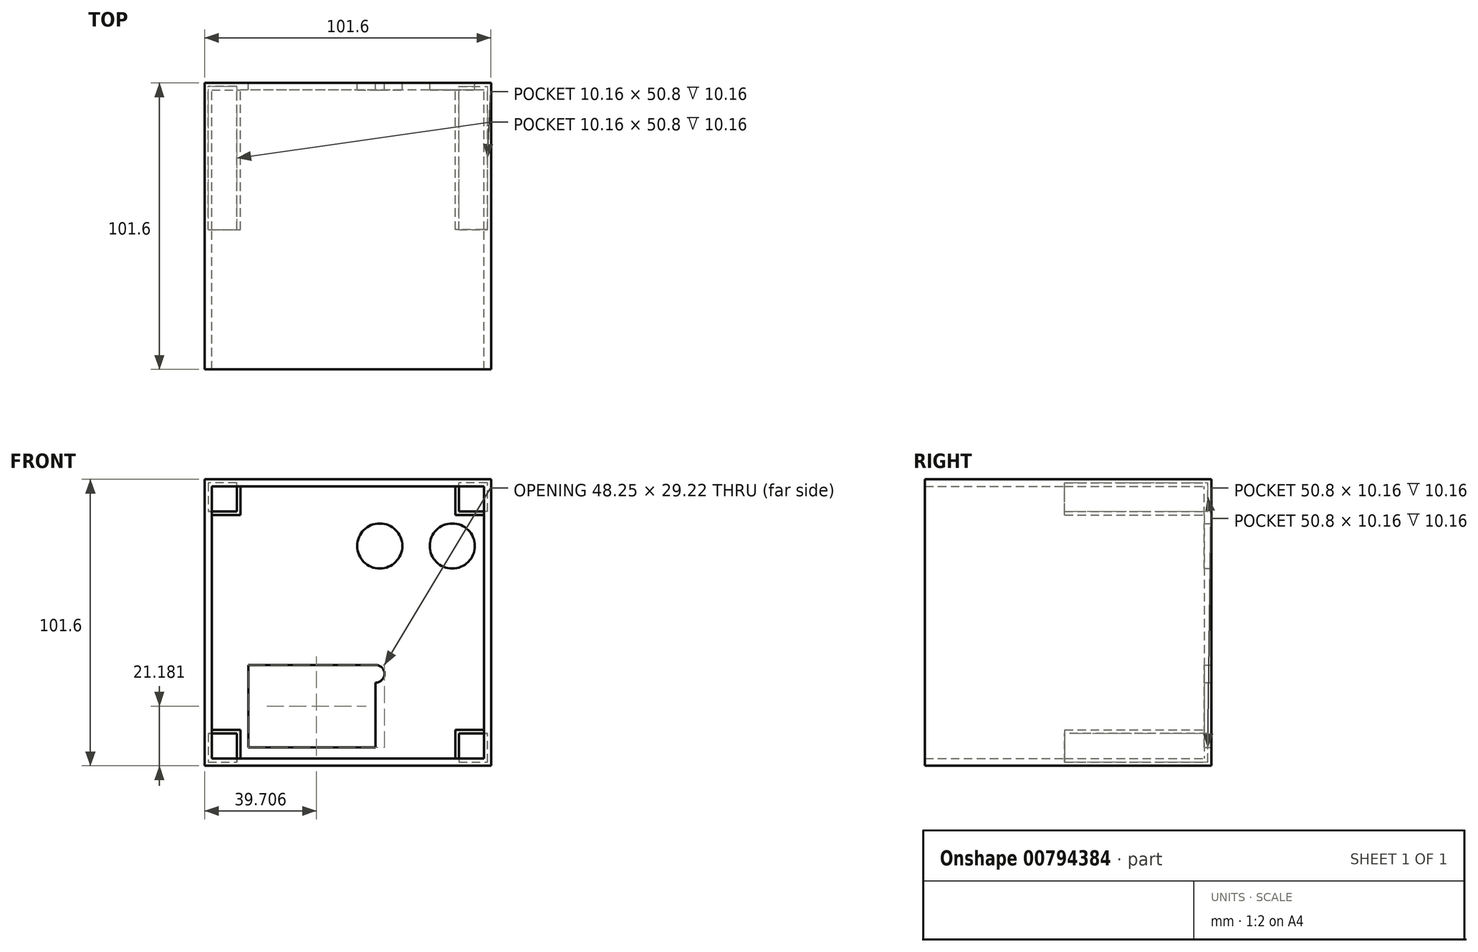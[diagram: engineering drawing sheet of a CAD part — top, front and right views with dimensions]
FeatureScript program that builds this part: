
annotation { "Feature Type Name" : "Feature", "Feature Type Description" : "" }
export const myFeature = defineFeature(function(context is Context, id is Id, definition is map)
    precondition{}
    {
        {
            var Q0;
            Q0=qCreatedBy(makeId("Front.planeOp"),FACE);
            var sketch = newSketch(context, id + "F0", { "sketchPlane" : qUnion([Q0])});
            skLineSegment(sketch, "E0", {"start": v(-90.78, 89.85) * mm, "end": v(-90.78, -11.75) * mm});
            skLineSegment(sketch, "E1", {"start": v(-90.78, -11.75) * mm, "end": v(10.82, -11.75) * mm});
            skLineSegment(sketch, "E2", {"start": v(10.82, -11.75) * mm, "end": v(10.82, 89.85) * mm});
            skLineSegment(sketch, "E3", {"start": v(10.82, 89.85) * mm, "end": v(-90.78, 89.85) * mm});
            skCircle(sketch, "E4", {"center": v(-28.63, 66.22) * mm, "radius": 8 * mm});
            skCircle(sketch, "E5", {"center": v(-2.9, 66.22) * mm, "radius": 8 * mm});
            skLineSegment(sketch, "E6", {"start": v(-75.2, 24.04) * mm, "end": v(-75.2, -5.18) * mm});
            skLineSegment(sketch, "E7", {"start": v(-75.2, -5.18) * mm, "end": v(-30.1, -5.18) * mm});
            skLineSegment(sketch, "E8", {"start": v(-30.1, -5.18) * mm, "end": v(-30.1, 24.04) * mm});
            skLineSegment(sketch, "E9", {"start": v(-30.1, 24.04) * mm, "end": v(-75.2, 24.04) * mm});
            skArc(sketch, "E10", {"start": v(-30.1, 17.74) * mm, "mid": v(-26.95, 20.9) * mm, "end": v(-30.1, 24.04) * mm});
            skLineSegment(sketch, "E11", {"start": v(-90.78, 77.15) * mm, "end": v(-78.08, 77.15) * mm});
            skLineSegment(sketch, "E12", {"start": v(-78.08, 77.15) * mm, "end": v(-78.08, 89.85) * mm});
            skLineSegment(sketch, "E13", {"start": v(-39.98, 89.85) * mm, "end": v(-39.98, -11.75) * mm, "construction": true});
            skLineSegment(sketch, "E14.MirrorCS", {"start": v(-1.88, 77.15) * mm, "end": v(-1.88, 89.85) * mm});
            skLineSegment(sketch, "E15.MirrorCS", {"start": v(10.82, 77.15) * mm, "end": v(-1.88, 77.15) * mm});
            skLineSegment(sketch, "E16", {"start": v(-90.78, 39.05) * mm, "end": v(10.82, 39.05) * mm, "construction": true});
            skLineSegment(sketch, "E17.MirrorCS", {"start": v(-90.78, 0.95) * mm, "end": v(-78.08, 0.95) * mm});
            skLineSegment(sketch, "E18.MirrorCS", {"start": v(-78.08, 0.95) * mm, "end": v(-78.08, -11.75) * mm});
            skLineSegment(sketch, "E19.MirrorCS", {"start": v(10.82, 0.95) * mm, "end": v(-1.88, 0.95) * mm});
            skLineSegment(sketch, "E20.MirrorCS", {"start": v(-1.88, 0.95) * mm, "end": v(-1.88, -11.75) * mm});
            skSolve(sketch);
        }
        {
            var Q0;
            {var subQ4=sQuery(id+"F0.wireOp",EDGE,"E19.MirrorCS");Q0=makeQuery(id+"F0.imprint","IMPRINT",FACE,{"disambiguationData":[TD([[makeQuery(id+"F0.imprint","IMPRINT",EDGE,{"derivedFrom":subQ4}),1.0]])]});}
            var Q1;
            {var subQ4=sQuery(id+"F0.wireOp",EDGE,"E14.MirrorCS");Q1=makeQuery(id+"F0.imprint","IMPRINT",FACE,{"disambiguationData":[TD([[makeQuery(id+"F0.imprint","IMPRINT",EDGE,{"derivedFrom":subQ4}),-1.0]])]});}
            var Q2;
            {var subQ3=sQuery(id+"F0.wireOp",EDGE,"E17.MirrorCS");Q2=makeQuery(id+"F0.imprint","IMPRINT",FACE,{"disambiguationData":[TD([[makeQuery(id+"F0.imprint","IMPRINT",EDGE,{"derivedFrom":subQ3}),-1.0]])]});}
            var Q3;
            {var subQ3=sQuery(id+"F0.wireOp",EDGE,"E11");Q3=makeQuery(id+"F0.imprint","IMPRINT",FACE,{"disambiguationData":[TD([[makeQuery(id+"F0.imprint","IMPRINT",EDGE,{"derivedFrom":subQ3}),1.0]])]});}
            var Q4;
            Q4=makeQuery(id+"F0.imprint","IMPRINT",FACE,{"disambiguationData":[TD([[makeQuery(id+"F0.imprint","IMPRINT",EDGE,{"derivedFrom":sQuery(id+"F0.wireOp",EDGE,"E4")}),-1.0]])]});
            extrude(context, id + "F1", {"entities" : qUnion([Q0, Q1, Q2, Q3, Q4]), "depth" : 101.6 * mm, "offsetDistance" : 25.4 * mm});
        }
        {
            var Q0;
            Q0=makeQuery(id+"F1.opExtrude","SWEPT_FACE",FACE,{"disambiguationData":[OSD([sQuery(id+"F0.wireOp",EDGE,"E4")])]});
            var Q1;
            Q1=makeQuery(id+"F1.opExtrude","SWEPT_FACE",FACE,{"disambiguationData":[OSD([sQuery(id+"F0.wireOp",EDGE,"E5")])]});
            var Q2;
            Q2=makeQuery(id+"F1.opExtrude","SWEPT_FACE",FACE,{"disambiguationData":[OSD([sQuery(id+"F0.wireOp",EDGE,"E9")])]});
            var Q3;
            Q3=makeQuery(id+"F1.opExtrude","SWEPT_FACE",FACE,{"disambiguationData":[OSD([sQuery(id+"F0.wireOp",EDGE,"E6")])]});
            var Q4;
            Q4=makeQuery(id+"F1.opExtrude","SWEPT_FACE",FACE,{"disambiguationData":[OSD([sQuery(id+"F0.wireOp",EDGE,"E8")])]});
            var Q5;
            Q5=makeQuery(id+"F1.opExtrude","SWEPT_FACE",FACE,{"disambiguationData":[OSD([sQuery(id+"F0.wireOp",EDGE,"E7")])]});
            var Q6;
            Q6=makeQuery(id+"F1.opExtrude","SWEPT_FACE",FACE,{"disambiguationData":[OSD([sQuery(id+"F0.wireOp",EDGE,"E10")])]});
            var Q7;
            Q7=makeQuery(id+"F1.opExtrude","CAP_FACE",FACE,{"disambiguationData":[OSD([sQuery(id+"F0.wireOp",EDGE,"E0"),sQuery(id+"F0.wireOp",EDGE,"E1"),sQuery(id+"F0.wireOp",EDGE,"E2"),sQuery(id+"F0.wireOp",EDGE,"E3"),sQuery(id+"F0.wireOp",EDGE,"E4"),sQuery(id+"F0.wireOp",EDGE,"E5"),sQuery(id+"F0.wireOp",EDGE,"E6"),sQuery(id+"F0.wireOp",EDGE,"E7"),sQuery(id+"F0.wireOp",EDGE,"E8"),sQuery(id+"F0.wireOp",EDGE,"E9"),sQuery(id+"F0.wireOp",EDGE,"E10")])],"isStart":false});
            shell(context, id + "F2", {"entities" : qUnion([Q0, Q1, Q2, Q3, Q4, Q5, Q6, Q7]), "thickness" : 2.54 * mm});
        }
        {
            var Q0;
            Q0=makeQuery(id+"F2.opShell","OFFSET_FACE",FACE,{"disambiguationData":[OSD([sQuery(id+"F0.wireOp",EDGE,"E0"),sQuery(id+"F0.wireOp",EDGE,"E1"),sQuery(id+"F0.wireOp",EDGE,"E2"),sQuery(id+"F0.wireOp",EDGE,"E3"),sQuery(id+"F0.wireOp",EDGE,"E4"),sQuery(id+"F0.wireOp",EDGE,"E5"),sQuery(id+"F0.wireOp",EDGE,"E6"),sQuery(id+"F0.wireOp",EDGE,"E7"),sQuery(id+"F0.wireOp",EDGE,"E8"),sQuery(id+"F0.wireOp",EDGE,"E9"),sQuery(id+"F0.wireOp",EDGE,"E10")])]});
            var sketch = newSketch(context, id + "F3", { "sketchPlane" : qUnion([Q0])});
            skLineSegment(sketch, "E21.0", {"start": v(-78.08, 77.15) * mm, "end": v(-78.08, 89.85) * mm});
            skLineSegment(sketch, "E22.0", {"start": v(-90.78, 77.15) * mm, "end": v(-78.08, 77.15) * mm});
            skPoint(sketch, "E23.0", {"position": v(-1.88, 83.5) * mm});
            skPoint(sketch, "E24.0", {"position": v(4.47, 77.15) * mm});
            skLineSegment(sketch, "E25.0", {"start": v(-90.78, 0.95) * mm, "end": v(-78.08, 0.95) * mm});
            skPoint(sketch, "E26.0", {"position": v(-78.08, -5.4) * mm});
            skLineSegment(sketch, "E27.0", {"start": v(-78.08, 0.95) * mm, "end": v(-78.08, -11.75) * mm});
            skLineSegment(sketch, "E28.0", {"start": v(-1.88, 0.95) * mm, "end": v(-1.88, -11.75) * mm});
            skPoint(sketch, "E29.0", {"position": v(4.47, 0.95) * mm});
            skLineSegment(sketch, "E30.0", {"start": v(10.82, 0.95) * mm, "end": v(-1.88, 0.95) * mm});
            skLineSegment(sketch, "E31.0", {"start": v(10.82, 89.85) * mm, "end": v(-90.78, 89.85) * mm});
            skLineSegment(sketch, "E32.0", {"start": v(-90.78, 89.85) * mm, "end": v(-90.78, -11.75) * mm});
            skLineSegment(sketch, "E33.0.0", {"start": v(10.82, -11.75) * mm, "end": v(10.82, 89.85) * mm});
            skLineSegment(sketch, "E33.0.3", {"start": v(-90.78, -11.75) * mm, "end": v(10.82, -11.75) * mm});
            skLineSegment(sketch, "E34.0", {"start": v(-1.88, 77.15) * mm, "end": v(-1.88, 89.85) * mm});
            skLineSegment(sketch, "E35.0", {"start": v(10.82, 77.15) * mm, "end": v(-1.88, 77.15) * mm});
            skSolve(sketch);
        }
        {
            var Q0;
            {var subQ0=sQuery(id+"F3.wireOp",EDGE,"E22.0");var subQ1=sQuery(id+"F3.wireOp",EDGE,"E21.0");var subQ2=makeQuery(id+"F3.imprint","INTERSECT",VERTEX,{"derivedFrom":[subQ1,subQ0]});Q0=makeQuery(id+"F3.imprint","IMPRINT",FACE,{"disambiguationData":[TD([[makeQuery(id+"F3.imprint","IMPRINT",EDGE,{"disambiguationData":[TD([[subQ2,-1.0]])],"derivedFrom":subQ1}),1.0]])]});}
            var Q1;
            {var subQ0=sQuery(id+"F3.wireOp",EDGE,"E35.0");var subQ1=sQuery(id+"F3.wireOp",EDGE,"E34.0");var subQ2=makeQuery(id+"F3.imprint","INTERSECT",VERTEX,{"derivedFrom":[subQ1,subQ0]});Q1=makeQuery(id+"F3.imprint","IMPRINT",FACE,{"disambiguationData":[TD([[makeQuery(id+"F3.imprint","IMPRINT",EDGE,{"disambiguationData":[TD([[subQ2,-1.0]])],"derivedFrom":subQ1}),-1.0]])]});}
            var Q2;
            {var subQ0=sQuery(id+"F3.wireOp",EDGE,"E27.0");var subQ1=sQuery(id+"F3.wireOp",EDGE,"E25.0");var subQ2=makeQuery(id+"F3.imprint","INTERSECT",VERTEX,{"derivedFrom":[subQ1,subQ0]});Q2=makeQuery(id+"F3.imprint","IMPRINT",FACE,{"disambiguationData":[TD([[makeQuery(id+"F3.imprint","IMPRINT",EDGE,{"disambiguationData":[TD([[subQ2,1.0]])],"derivedFrom":subQ1}),-1.0]])]});}
            var Q3;
            {var subQ0=sQuery(id+"F3.wireOp",EDGE,"E30.0");var subQ1=sQuery(id+"F3.wireOp",EDGE,"E28.0");var subQ2=makeQuery(id+"F3.imprint","INTERSECT",VERTEX,{"derivedFrom":[subQ1,subQ0]});Q3=makeQuery(id+"F3.imprint","IMPRINT",FACE,{"disambiguationData":[TD([[makeQuery(id+"F3.imprint","IMPRINT",EDGE,{"disambiguationData":[TD([[subQ2,-1.0]])],"derivedFrom":subQ1}),1.0]])]});}
            extrude(context, id + "F4", {"entities" : qUnion([Q0, Q1, Q2, Q3]), "operationType" : NewBodyOperationType.ADD, "depth" : 49.53 * mm, "offsetDistance" : 25.4 * mm});
        }
        {
            var Q0;
            Q0=makeQuery(id+"F4.opExtrude","CAP_FACE",FACE,{"disambiguationData":[OSD([sQuery(id+"F0.wireOp",EDGE,"E0"),sQuery(id+"F0.wireOp",EDGE,"E3"),sQuery(id+"F3.wireOp",EDGE,"E21.0"),sQuery(id+"F3.wireOp",EDGE,"E22.0")])],"isStart":false});
            var Q1;
            Q1=makeQuery(id+"F4.opExtrude","CAP_FACE",FACE,{"disambiguationData":[OSD([sQuery(id+"F0.wireOp",EDGE,"E2"),sQuery(id+"F0.wireOp",EDGE,"E3"),sQuery(id+"F3.wireOp",EDGE,"E34.0"),sQuery(id+"F3.wireOp",EDGE,"E35.0")])],"isStart":false});
            var Q2;
            Q2=makeQuery(id+"F4.opExtrude","CAP_FACE",FACE,{"disambiguationData":[OSD([sQuery(id+"F0.wireOp",EDGE,"E0"),sQuery(id+"F0.wireOp",EDGE,"E1"),sQuery(id+"F3.wireOp",EDGE,"E25.0"),sQuery(id+"F3.wireOp",EDGE,"E27.0")])],"isStart":false});
            var Q3;
            Q3=makeQuery(id+"F4.opExtrude","CAP_FACE",FACE,{"disambiguationData":[OSD([sQuery(id+"F0.wireOp",EDGE,"E1"),sQuery(id+"F0.wireOp",EDGE,"E2"),sQuery(id+"F3.wireOp",EDGE,"E28.0"),sQuery(id+"F3.wireOp",EDGE,"E30.0")])],"isStart":false});
            shell(context, id + "F5", {"entities" : qUnion([Q0, Q1, Q2, Q3]), "thickness" : 1.27 * mm});
        }
    });
